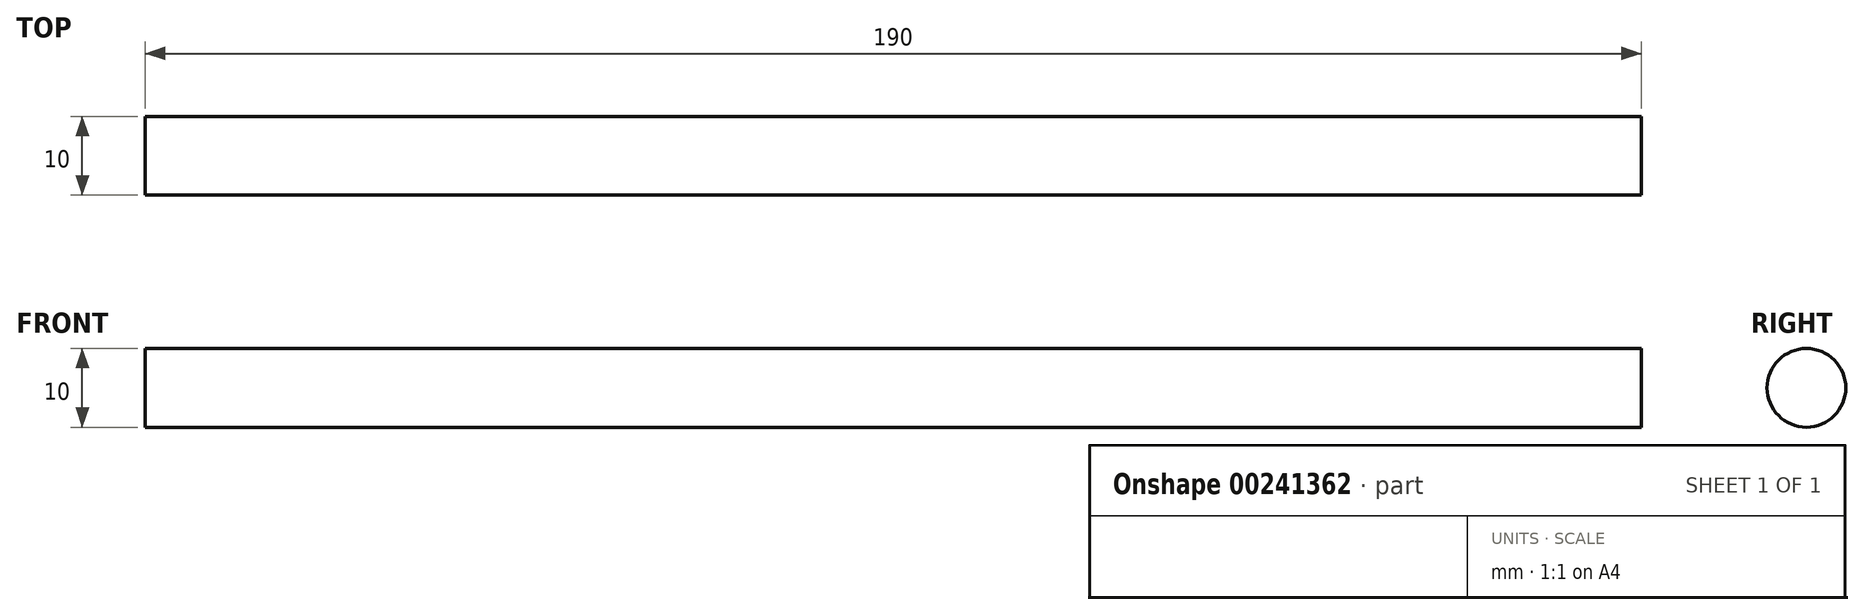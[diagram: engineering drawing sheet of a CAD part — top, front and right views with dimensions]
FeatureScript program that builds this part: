
annotation { "Feature Type Name" : "Feature", "Feature Type Description" : "" }
export const myFeature = defineFeature(function(context is Context, id is Id, definition is map)
    precondition{}
    {
        {
            var Q0;
            Q0=qCreatedBy(makeId("Right.planeOp"),FACE);
            var sketch = newSketch(context, id + "F0", { "sketchPlane" : qUnion([Q0])});
            skCircle(sketch, "E0", {"center": v(0, 0) * mm, "radius": 5 * mm});
            skSolve(sketch);
        }
        {
            var Q0;
            Q0 = qSketchRegion(id + "F0", true);
            extrude(context, id + "F1", {"entities" : qUnion([Q0]), "depth" : 190 * mm});
        }
    });
